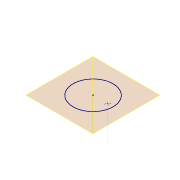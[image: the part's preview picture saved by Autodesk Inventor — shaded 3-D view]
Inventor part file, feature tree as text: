
AUTODESK INVENTOR PART (.ipt)
format: ipt  version: 2016 (Build 200138000, 138)  size: 67,072 bytes
history: native  units: in
note: dims shown in document units (in); Inventor stores cm internally (conversion verified against a paired STEP export)
features: other x6, plane x1, sketch x1
ambient origin geometry x8: Origin, YZ Plane, XZ Plane, XY Plane, X Axis, Y Axis, Z Axis, Center Point
feature tree (8):
  other  "skeleton.ipt"
  other  "Blocks"
  plane  "Work Plane1"
  other  "Work Axis1"
  other  "Work Axis2"
  other  "L2_foot"
  sketch  "Sketch2"  dims[d1=0.3937in d0=2.3622in d2=9.4488in d5=1.9291in d6=5.9055in]
  other  "L2_foot:1"
